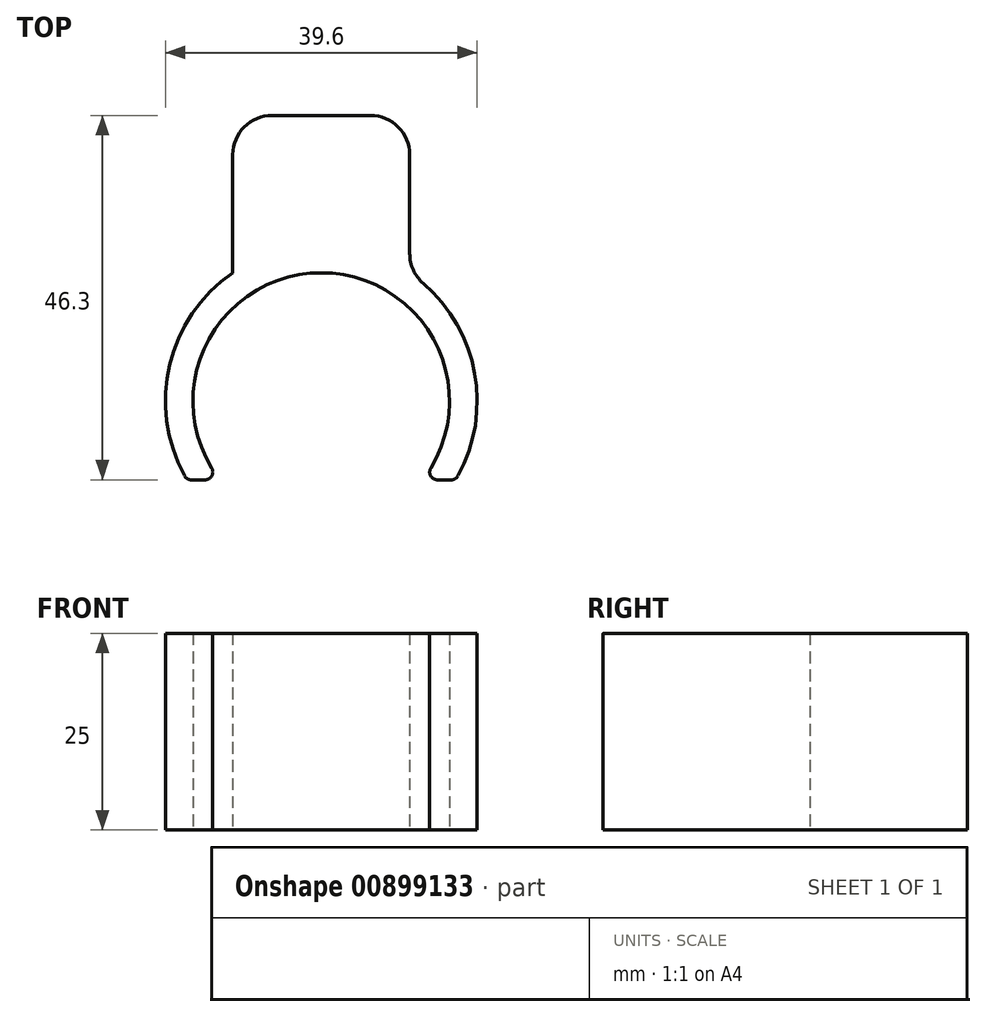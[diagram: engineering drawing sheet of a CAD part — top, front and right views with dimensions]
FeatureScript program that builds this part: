
annotation { "Feature Type Name" : "Feature", "Feature Type Description" : "" }
export const myFeature = defineFeature(function(context is Context, id is Id, definition is map)
    precondition{}
    {
        {
            var Q0;
            Q0=qCreatedBy(makeId("Top.planeOp"),FACE);
            var sketch = newSketch(context, id + "F0", { "sketchPlane" : qUnion([Q0])});
            skArc(sketch, "E0", {"start": v(12.87, -10) * mm, "mid": v(0, 16.3) * mm, "end": v(-12.87, -10) * mm});
            skArc(sketch, "E1", {"start": v(17.09, -10) * mm, "mid": v(0, 19.8) * mm, "end": v(-17.09, -10) * mm});
            skLineSegment(sketch, "E2", {"start": v(-17.09, -10) * mm, "end": v(-12.87, -10) * mm});
            skLineSegment(sketch, "E3.trimOffspring", {"start": v(12.87, -10) * mm, "end": v(17.09, -10) * mm});
            skSolve(sketch);
        }
        {
            var Q0;
            Q0 = qSketchRegion(id + "F0", true);
            extrude(context, id + "F1", {"entities" : qUnion([Q0]), "depth" : 25 * mm, "offsetDistance" : 25 * mm});
        }
        {
            var Q0;
            Q0=makeQuery(id+"F1.opExtrude","CAP_FACE",FACE,{"disambiguationData":[OSD([sQuery(id+"F0.wireOp",EDGE,"E0"),sQuery(id+"F0.wireOp",EDGE,"E1"),sQuery(id+"F0.wireOp",EDGE,"E2"),sQuery(id+"F0.wireOp",EDGE,"E3.trimOffspring")])],"isStart":true});
            var sketch = newSketch(context, id + "F2", { "sketchPlane" : qUnion([Q0])});
            skLineSegment(sketch, "E4", {"start": v(0, -16.3) * mm, "end": v(11.24, -16.3) * mm});
            skLineSegment(sketch, "E5", {"start": v(11.24, -16.3) * mm, "end": v(11.24, -36.3) * mm});
            skLineSegment(sketch, "E6", {"start": v(11.24, -36.3) * mm, "end": v(-11.24, -36.3) * mm});
            skLineSegment(sketch, "E7", {"start": v(-11.24, -36.3) * mm, "end": v(-11.24, -16.3) * mm});
            skLineSegment(sketch, "E8", {"start": v(-11.24, -16.3) * mm, "end": v(0, -16.3) * mm});
            skLineSegment(sketch, "E9", {"start": v(0, -16.3) * mm, "end": v(0, -36.3) * mm, "construction": true});
            skSolve(sketch);
        }
        {
            var Q0;
            Q0 = qSketchRegion(id + "F2", true);
            var Q1;
            Q1=makeQuery(id+"F1.opExtrude","CAP_FACE",FACE,{"disambiguationData":[OSD([sQuery(id+"F0.wireOp",EDGE,"E0"),sQuery(id+"F0.wireOp",EDGE,"E1"),sQuery(id+"F0.wireOp",EDGE,"E2"),sQuery(id+"F0.wireOp",EDGE,"E3.trimOffspring")])],"isStart":false});
            extrude(context, id + "F3", {"entities" : qUnion([Q0]), "operationType" : NewBodyOperationType.ADD, "endBound" : BoundingType.UP_TO_SURFACE, "oppositeDirection" : true, "depth" : 25 * mm, "endBoundEntityFace" : qUnion([Q1]), "offsetDistance" : 25 * mm});
        }
        {
            var Q0;
            Q0=makeQuery(id+"F1.opExtrude","SWEPT_EDGE",EDGE,{"disambiguationData":[OSD([sQuery(id+"F0.wireOp",EDGE,"E0"),sQuery(id+"F0.wireOp",EDGE,"E2")])]});
            var Q1;
            Q1=makeQuery(id+"F1.opExtrude","SWEPT_EDGE",EDGE,{"disambiguationData":[OSD([sQuery(id+"F0.wireOp",EDGE,"E0"),sQuery(id+"F0.wireOp",EDGE,"E3.trimOffspring")])]});
            var Q2;
            Q2=makeQuery(id+"F1.opExtrude","SWEPT_EDGE",EDGE,{"disambiguationData":[OSD([sQuery(id+"F0.wireOp",EDGE,"E1"),sQuery(id+"F0.wireOp",EDGE,"E2")])]});
            var Q3;
            Q3=makeQuery(id+"F1.opExtrude","SWEPT_EDGE",EDGE,{"disambiguationData":[OSD([sQuery(id+"F0.wireOp",EDGE,"E1"),sQuery(id+"F0.wireOp",EDGE,"E3.trimOffspring")])]});
            fillet(context, id + "F4", {"entities" : qUnion([Q0, Q1, Q2, Q3]), "radius" : 1 * mm, "tangentPropagation" : true, "allowEdgeOverflow" : false});
        }
        {
            var Q0;
            Q0=makeQuery(id+"F3.opExtrude","SWEPT_EDGE",EDGE,{"disambiguationData":[OSD([sQuery(id+"F0.wireOp",EDGE,"E1"),sQuery(id+"F2.wireOp",EDGE,"E7"),sQuery(id+"F2.wireOp",EDGE,"E8")])]});
            var Q1;
            Q1=makeQuery(id+"F3.opExtrude","SWEPT_EDGE",EDGE,{"disambiguationData":[OSD([sQuery(id+"F0.wireOp",EDGE,"E1"),sQuery(id+"F2.wireOp",EDGE,"E4"),sQuery(id+"F2.wireOp",EDGE,"E5")])]});
            var Q2;
            Q2=makeQuery(id+"F3.opExtrude","SWEPT_EDGE",EDGE,{"disambiguationData":[OSD([sQuery(id+"F2.wireOp",EDGE,"E6"),sQuery(id+"F2.wireOp",EDGE,"E7")])]});
            var Q3;
            Q3=makeQuery(id+"F3.opExtrude","SWEPT_EDGE",EDGE,{"disambiguationData":[OSD([sQuery(id+"F2.wireOp",EDGE,"E5"),sQuery(id+"F2.wireOp",EDGE,"E6")])]});
            fillet(context, id + "F5", {"entities" : qUnion([Q0, Q1, Q2, Q3]), "radius" : 5 * mm, "tangentPropagation" : true, "allowEdgeOverflow" : false});
        }
    });
